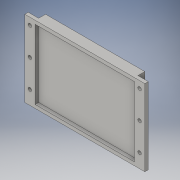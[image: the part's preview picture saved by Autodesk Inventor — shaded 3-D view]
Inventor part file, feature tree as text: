
AUTODESK INVENTOR PART (.ipt)
format: ipt  version: 2016 (Build 200138000, 138)  size: 169,472 bytes
history: native  units: in
note: dims shown in document units (in); Inventor stores cm internally (conversion verified against a paired STEP export)
features: sketch x7, hole x4, extrude x3
ambient origin geometry x8: Origin, YZ Plane, XZ Plane, XY Plane, X Axis, Y Axis, Z Axis, Center Point
bodies: Solid1 (feature_tree)
feature tree (14):
  extrude  "Extrusion1"  Depth=0.75in
  hole  "Hole1"  [1 undecoded]
  extrude  "Extrusion2"  TaperAngle=0.0deg  [1 undecoded]
  extrude  "Extrusion3"  Depth=1.0in
  hole  "Hole2"  [1 undecoded]
  hole  "Hole3"  [1 undecoded]
  hole  "Hole4"  [1 undecoded]
  sketch  "Sketch1"  dims[d0=8.65in d1=0.75in]
  sketch  "Sketch2"  dims[d2=5.5in d3=0.0in d4=0.0in]
  sketch  "Sketch3"  dims[d5=0.0in d6=0.0in]
  sketch  "Sketch6"  dims[d7=0.0in d8=1.0in]
  sketch  "Sketch7"  dims[d10=0.375in d11=0.375in]
  sketch  "Sketch8"  dims[d12=0.25in d13=0.75in d14=0.375in d15=0.25in d16=0.5635in d17=1.0in d18=0.8108in d19=0.75in]
  sketch  "Sketch9"  dims[d20=0.75in d21=0.25in d22=0.25in d23=0.25in d24=0.0in d25=0.0in d26=0.5in d27=0.0in d28=0.75in d32=0.75in d33=0.0in d34=0.25in d35=10.0in d36=0.0in d37=2.0in d38=0.375in d39=2.0in d40=0.375in d41=0.1935in d42=0.75in d43=0.375in d44=0.25in d45=0.5635in d46=1.0in d47=0.8108in d48=4.5in d49=0.375in d50=0.1935in d51=0.75in d52=0.375in d53=0.25in d54=0.5635in d55=1.0in d56=0.8108in d57=2.0in d58=0.0in d59=2.0in d60=0.375in d61=0.375in d62=0.25in d63=0.75in d64=0.375in d65=0.25in d66=0.5635in d67=1.0in d68=0.8108in]
note: 5 required parameter values undecoded (feature->parameter linkage not recoverable at this tier; creation-order binding heuristic only, values carry confidence <= 0.55)
